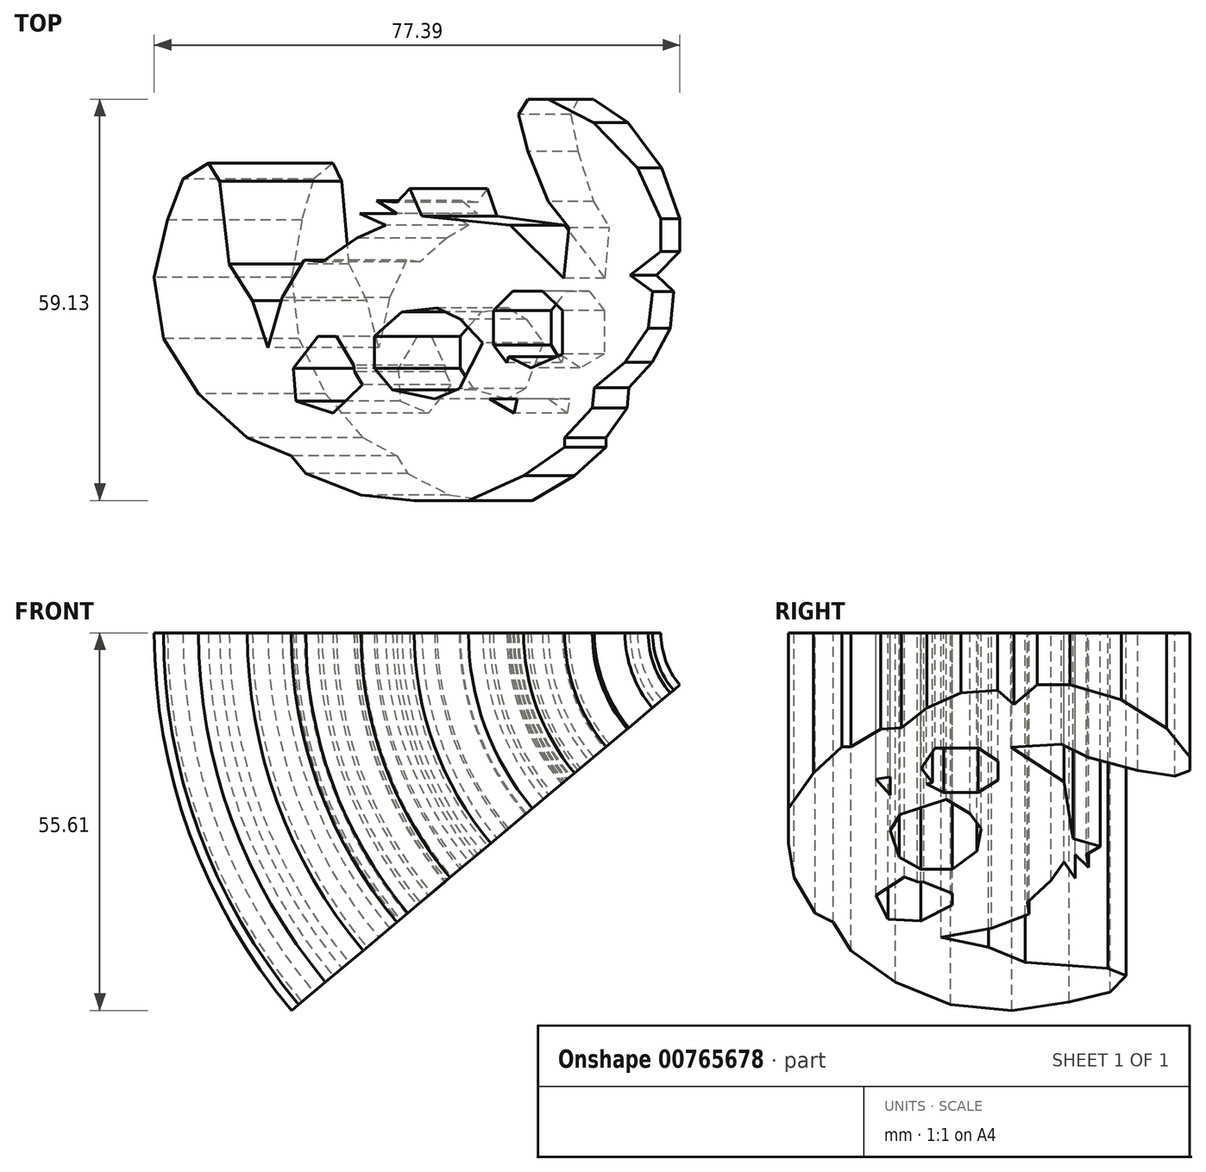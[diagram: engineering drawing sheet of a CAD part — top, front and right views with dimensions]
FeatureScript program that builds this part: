
annotation { "Feature Type Name" : "Feature", "Feature Type Description" : "" }
export const myFeature = defineFeature(function(context is Context, id is Id, definition is map)
    precondition{}
    {
        {
            var Q0;
            Q0=qCreatedBy(makeId("Top.planeOp"),FACE);
            var sketch = newSketch(context, id + "F0", { "sketchPlane" : qUnion([Q0])});
            skLineSegment(sketch, "E0", {"start": v(26.54, 9.5) * mm, "end": v(28.8, 12.82) * mm});
            skLineSegment(sketch, "E1", {"start": v(28.8, 12.82) * mm, "end": v(35.13, 21.56) * mm});
            skLineSegment(sketch, "E2", {"start": v(35.13, 21.56) * mm, "end": v(31.82, 23.96) * mm});
            skLineSegment(sketch, "E3", {"start": v(31.82, 23.96) * mm, "end": v(36.34, 27.44) * mm});
            skLineSegment(sketch, "E4", {"start": v(36.34, 27.44) * mm, "end": v(36.34, 32.26) * mm});
            skLineSegment(sketch, "E5", {"start": v(36.34, 32.26) * mm, "end": v(32.87, 39.8) * mm});
            skLineSegment(sketch, "E6", {"start": v(32.87, 39.8) * mm, "end": v(26.39, 46.43) * mm});
            skLineSegment(sketch, "E7", {"start": v(26.39, 46.43) * mm, "end": v(19.76, 49.9) * mm});
            skLineSegment(sketch, "E8", {"start": v(19.76, 49.9) * mm, "end": v(16.74, 49.9) * mm});
            skLineSegment(sketch, "E9", {"start": v(16.74, 49.9) * mm, "end": v(15.39, 47.64) * mm});
            skLineSegment(sketch, "E10", {"start": v(15.39, 47.64) * mm, "end": v(16.74, 42.21) * mm});
            skLineSegment(sketch, "E11", {"start": v(16.74, 42.21) * mm, "end": v(19.76, 34.82) * mm});
            skLineSegment(sketch, "E12", {"start": v(19.76, 34.82) * mm, "end": v(24.13, 29.25) * mm});
            skLineSegment(sketch, "E13", {"start": v(24.13, 29.25) * mm, "end": v(28.8, 21.56) * mm});
            skLineSegment(sketch, "E14", {"start": v(28.8, 21.56) * mm, "end": v(28.8, 12.82) * mm});
            skLineSegment(sketch, "E15", {"start": v(26.54, 7.4) * mm, "end": v(31.06, 11.16) * mm});
            skLineSegment(sketch, "E16", {"start": v(31.06, 11.16) * mm, "end": v(34.47, 16.16) * mm});
            skLineSegment(sketch, "E17", {"start": v(34.47, 16.16) * mm, "end": v(35.13, 21.56) * mm});
            skLineSegment(sketch, "E18", {"start": v(22.17, 0) * mm, "end": v(26.24, 4.38) * mm});
            skLineSegment(sketch, "E19", {"start": v(26.24, 4.38) * mm, "end": v(26.54, 7.4) * mm});
            skLineSegment(sketch, "E20", {"start": v(26.54, 11.46) * mm, "end": v(24.73, 17.5) * mm});
            skLineSegment(sketch, "E21", {"start": v(24.73, 17.5) * mm, "end": v(22.02, 23.52) * mm});
            skLineSegment(sketch, "E22", {"start": v(22.02, 23.52) * mm, "end": v(22.78, 30.97) * mm});
            skLineSegment(sketch, "E23", {"start": v(22.02, 23.52) * mm, "end": v(14.18, 31.36) * mm});
            skLineSegment(sketch, "E24", {"start": v(14.18, 31.36) * mm, "end": v(5.36, 32.26) * mm});
            skLineSegment(sketch, "E25", {"start": v(5.36, 32.26) * mm, "end": v(1.15, 32.7) * mm});
            skLineSegment(sketch, "E26", {"start": v(1.15, 32.7) * mm, "end": v(-0.65, 36.71) * mm});
            skLineSegment(sketch, "E27", {"start": v(-0.65, 36.71) * mm, "end": v(-2.55, 34.67) * mm});
            skLineSegment(sketch, "E28", {"start": v(-2.55, 34.67) * mm, "end": v(-5.52, 34.98) * mm});
            skLineSegment(sketch, "E29", {"start": v(-5.52, 34.98) * mm, "end": v(-2.55, 33.02) * mm});
            skLineSegment(sketch, "E30", {"start": v(-2.55, 33.02) * mm, "end": v(-7.98, 33.02) * mm});
            skLineSegment(sketch, "E31", {"start": v(-7.98, 33.02) * mm, "end": v(-4.2, 31.36) * mm});
            skLineSegment(sketch, "E32", {"start": v(-4.2, 31.36) * mm, "end": v(-8.43, 29.46) * mm});
            skLineSegment(sketch, "E33", {"start": v(-8.43, 29.46) * mm, "end": v(-13.55, 25.93) * mm});
            skLineSegment(sketch, "E34", {"start": v(-13.55, 25.93) * mm, "end": v(-16.2, 26.2) * mm});
            skLineSegment(sketch, "E35", {"start": v(-16.2, 26.2) * mm, "end": v(-19.43, 20.66) * mm});
            skLineSegment(sketch, "E36", {"start": v(-19.43, 20.66) * mm, "end": v(-21.54, 13.27) * mm});
            skLineSegment(sketch, "E37", {"start": v(-21.54, 13.27) * mm, "end": v(-21.54, 6.49) * mm});
            skLineSegment(sketch, "E38", {"start": v(-21.54, 6.49) * mm, "end": v(-20.18, 0) * mm});
            skLineSegment(sketch, "E39", {"start": v(-20.18, 0) * mm, "end": v(-15.96, -5.27) * mm});
            skLineSegment(sketch, "E40", {"start": v(-15.96, -5.27) * mm, "end": v(-7.82, -8.43) * mm});
            skLineSegment(sketch, "E41", {"start": v(-7.82, -8.43) * mm, "end": v(0, -9.23) * mm});
            skLineSegment(sketch, "E42", {"start": v(0, -9.23) * mm, "end": v(8, -9.23) * mm});
            skLineSegment(sketch, "E43", {"start": v(8, -9.23) * mm, "end": v(16.13, -5.58) * mm});
            skLineSegment(sketch, "E44", {"start": v(16.13, -5.58) * mm, "end": v(22.17, -1.35) * mm});
            skLineSegment(sketch, "E45", {"start": v(22.17, -1.35) * mm, "end": v(22.17, 0) * mm});
            skLineSegment(sketch, "E46", {"start": v(-21.54, 13.27) * mm, "end": v(-23.8, 20.2) * mm});
            skLineSegment(sketch, "E47", {"start": v(-23.8, 20.2) * mm, "end": v(-28.47, 27.6) * mm});
            skLineSegment(sketch, "E48", {"start": v(-27.23, 25.63) * mm, "end": v(-28.62, 37.84) * mm});
            skLineSegment(sketch, "E49", {"start": v(-28.62, 37.84) * mm, "end": v(-30.3, 40.5) * mm});
            skLineSegment(sketch, "E50", {"start": v(-30.3, 40.5) * mm, "end": v(-34.04, 38.13) * mm});
            skLineSegment(sketch, "E51", {"start": v(-34.04, 38.13) * mm, "end": v(-36.31, 32.11) * mm});
            skLineSegment(sketch, "E52", {"start": v(-36.31, 32.11) * mm, "end": v(-38.27, 23.67) * mm});
            skLineSegment(sketch, "E53", {"start": v(-38.27, 23.67) * mm, "end": v(-36.91, 14.63) * mm});
            skLineSegment(sketch, "E54", {"start": v(-36.91, 14.63) * mm, "end": v(-31.76, 6.49) * mm});
            skLineSegment(sketch, "E55", {"start": v(-31.76, 6.49) * mm, "end": v(-24.55, 0) * mm});
            skLineSegment(sketch, "E56", {"start": v(-24.55, 0) * mm, "end": v(-18.07, -2.63) * mm});
            skLineSegment(sketch, "E57", {"start": v(-4.36, 16.29) * mm, "end": v(-1.8, 18.55) * mm});
            skLineSegment(sketch, "E58", {"start": v(-1.8, 18.55) * mm, "end": v(3.4, 19.14) * mm});
            skLineSegment(sketch, "E59", {"start": v(3.4, 19.14) * mm, "end": v(6.8, 17.5) * mm});
            skLineSegment(sketch, "E60", {"start": v(6.8, 17.5) * mm, "end": v(10.11, 14.03) * mm});
            skLineSegment(sketch, "E61", {"start": v(10.11, 14.03) * mm, "end": v(6.64, 7.24) * mm});
            skLineSegment(sketch, "E62", {"start": v(6.64, 7.24) * mm, "end": v(3.03, 5.74) * mm});
            skLineSegment(sketch, "E63", {"start": v(3.03, 5.74) * mm, "end": v(-3.15, 7.1) * mm});
            skLineSegment(sketch, "E64", {"start": v(-3.15, 7.1) * mm, "end": v(-5.87, 10.26) * mm});
            skLineSegment(sketch, "E65", {"start": v(-5.87, 10.26) * mm, "end": v(-5.87, 14.93) * mm});
            skLineSegment(sketch, "E66", {"start": v(-5.87, 14.93) * mm, "end": v(-4.36, 16.29) * mm});
            skLineSegment(sketch, "E67", {"start": v(-3.15, 20.5) * mm, "end": v(0, 21.71) * mm});
            skLineSegment(sketch, "E68", {"start": v(0, 21.71) * mm, "end": v(2.57, 21.71) * mm});
            skLineSegment(sketch, "E69", {"start": v(9.77, 29.25) * mm, "end": v(11.87, 31.6) * mm});
            skPoint(sketch, "E69.startSnap0", {"position": v(9.77, 31.81) * mm});
            skLineSegment(sketch, "E70", {"start": v(11.87, 31.6) * mm, "end": v(11.77, 30.6) * mm});
            skLineSegment(sketch, "E71", {"start": v(16.67, 28.87) * mm, "end": v(12.82, 28.87) * mm});
            skLineSegment(sketch, "E72", {"start": v(12.82, 28.87) * mm, "end": v(9.88, 25.93) * mm});
            skLineSegment(sketch, "E73", {"start": v(9.88, 25.93) * mm, "end": v(9.88, 16.44) * mm});
            skLineSegment(sketch, "E74", {"start": v(9.88, 16.44) * mm, "end": v(9.88, 10.86) * mm});
            skLineSegment(sketch, "E75", {"start": v(9.88, 10.86) * mm, "end": v(14.87, 8.31) * mm});
            skLineSegment(sketch, "E76", {"start": v(14.87, 8.31) * mm, "end": v(17.5, 6.97) * mm});
            skLineSegment(sketch, "E77", {"start": v(17.5, 6.97) * mm, "end": v(22.02, 8.3) * mm});
            skLineSegment(sketch, "E78", {"start": v(22.02, 8.3) * mm, "end": v(24.94, 14.03) * mm});
            skLineSegment(sketch, "E79", {"start": v(24.94, 14.03) * mm, "end": v(24.88, 12.97) * mm});
            skLineSegment(sketch, "E80", {"start": v(-17.81, 20.66) * mm, "end": v(-15.04, 23.43) * mm});
            skPoint(sketch, "E80.startSnap0", {"position": v(-17.81, 23.43) * mm});
            skPoint(sketch, "E80.endSnap0", {"position": v(-17.81, 23.43) * mm});
            skLineSegment(sketch, "E81", {"start": v(-15.04, 23.43) * mm, "end": v(-10.95, 21.34) * mm});
            skLineSegment(sketch, "E82", {"start": v(-10.95, 21.34) * mm, "end": v(-6.5, 14.03) * mm});
            skLineSegment(sketch, "E83", {"start": v(-6.5, 14.03) * mm, "end": v(-5.87, 5.43) * mm});
            skLineSegment(sketch, "E84", {"start": v(-5.87, 5.43) * mm, "end": v(-10.54, 0.76) * mm});
            skLineSegment(sketch, "E85", {"start": v(-10.54, 0.76) * mm, "end": v(-15.96, 0.76) * mm});
            skLineSegment(sketch, "E86", {"start": v(-15.96, 0.76) * mm, "end": v(-20.95, 3.68) * mm});
            skLineSegment(sketch, "E87", {"start": v(-14.46, -1.65) * mm, "end": v(-6.92, 0) * mm});
            skLineSegment(sketch, "E88", {"start": v(-6.92, 0) * mm, "end": v(0, 3.93) * mm});
            skLineSegment(sketch, "E89", {"start": v(0, 3.93) * mm, "end": v(7.25, 5.74) * mm});
            skLineSegment(sketch, "E90", {"start": v(7.25, 5.74) * mm, "end": v(22.62, 5.74) * mm});
            skLineSegment(sketch, "E91", {"start": v(48.24, 51.49) * mm, "end": v(48.24, -7.38) * mm});
            skLineSegment(sketch, "E92", {"start": v(11.66, 13.65) * mm, "end": v(11.66, 18.74) * mm});
            skLineSegment(sketch, "E93", {"start": v(11.66, 18.74) * mm, "end": v(14.56, 21.64) * mm});
            skLineSegment(sketch, "E94", {"start": v(14.56, 21.64) * mm, "end": v(18.92, 21.64) * mm});
            skLineSegment(sketch, "E95", {"start": v(18.92, 21.64) * mm, "end": v(21.83, 18.74) * mm});
            skLineSegment(sketch, "E96", {"start": v(21.83, 18.74) * mm, "end": v(21.83, 12.38) * mm});
            skLineSegment(sketch, "E97", {"start": v(21.83, 12.38) * mm, "end": v(17.22, 10.3) * mm});
            skLineSegment(sketch, "E98", {"start": v(17.22, 10.3) * mm, "end": v(13.92, 12) * mm});
            skLineSegment(sketch, "E99", {"start": v(13.92, 12) * mm, "end": v(13.66, 11.1) * mm});
            skLineSegment(sketch, "E100", {"start": v(13.66, 11.1) * mm, "end": v(11.66, 13.65) * mm});
            skLineSegment(sketch, "E101", {"start": v(-14.14, 14.92) * mm, "end": v(-17.77, 10.26) * mm});
            skLineSegment(sketch, "E102", {"start": v(-17.77, 10.26) * mm, "end": v(-17.42, 5.43) * mm});
            skLineSegment(sketch, "E103", {"start": v(-17.42, 5.43) * mm, "end": v(-11.96, 3.66) * mm});
            skLineSegment(sketch, "E104", {"start": v(-14.14, 14.92) * mm, "end": v(-11.41, 14.92) * mm});
            skLineSegment(sketch, "E105", {"start": v(-11.41, 14.92) * mm, "end": v(-10.26, 13.02) * mm});
            skLineSegment(sketch, "E106", {"start": v(-10.26, 13.02) * mm, "end": v(-8.86, 10.71) * mm});
            skLineSegment(sketch, "E107", {"start": v(-8.86, 10.71) * mm, "end": v(-8.78, 9.73) * mm});
            skPoint(sketch, "E107.endSnap0", {"position": v(-6.18, 9.73) * mm});
            skLineSegment(sketch, "E108", {"start": v(-8.78, 9.73) * mm, "end": v(-7.64, 7.85) * mm});
            skLineSegment(sketch, "E109", {"start": v(-7.64, 7.85) * mm, "end": v(-11.96, 3.66) * mm});
            skLineSegment(sketch, "E110", {"start": v(11.11, 5.74) * mm, "end": v(14.75, 3.66) * mm});
            skLineSegment(sketch, "E111", {"start": v(14.75, 3.66) * mm, "end": v(15.2, 5.74) * mm});
            skLineSegment(sketch, "E112", {"start": v(12.38, -4.7) * mm, "end": v(14.56, 0) * mm});
            skPoint(sketch, "E112.startSnap0", {"position": v(12.38, 9.59) * mm});
            skLineSegment(sketch, "E113", {"start": v(14.56, 0) * mm, "end": v(17.56, -1.4) * mm});
            skLineSegment(sketch, "E114", {"start": v(-5.42, -5.97) * mm, "end": v(-2.7, -5.97) * mm});
            skSolve(sketch);
        }
        {
            var Q0;
            Q0 = qSketchRegion(id + "F0", true);
            var Q1;
            Q1=sQuery(id+"F0.wireOp",EDGE,"E91");
            revolve(context, id + "F1", {"surfaceOperationType" : NewSurfaceOperationType.NEW, "entities" : qUnion([Q0]), "axis" : qUnion([Q1]), "revolveType" : RevolveType.ONE_DIRECTION, "angle" : 40 * degree});
        }
    });
